# Revit family: РДК-50СВ
name_source: partatom
category: Арматура трубопроводов
units: mm (PartAtom-declared; Revit-internal decimal feet)

## family parameters
Всегда вертикально = Да
На основе рабочей плоскости = Нет
Общий = Нет
При загрузке вырезать с полостями = Нет
Размер круглого соединителя = Использовать диаметр
Тип детали = Клапан - Вставляется

## types (8) — shared parameters
ADSK_Единица измерения = шт.
ADSK_Завод-изготовитель = РУП "БЕЛГАЗТЕХНИКА"
ADSK_Количество = 1
ADSK_Марка = РДК-50СВ
ADSK_Масса_Текст = 24,0 кг
ADSK_Материал наименование = АК-12 ГОСТ 1583-93
ADSK_Тип соединения = фланцевый
zero-valued in all types: Отметка по умолчанию

## per-type parameters (varying)
| type | ADSK_Диапазоны настройки выходного давления, кПа | ADSK_Наименование | направление потока газа Л - влево | направление потока газа П - вправо |
| РДК-50СВ-Л 1,8-10 | 1,8-10 | Регулятор РДК-50СВ-Л-(1,8-10) ТУ BY 100270876.205-2020 | Да | Нет |
| РДК-50СВ-П 1,8-10 | 1,8-10 | Регулятор РДК-50СВ-П-(1,8-10) ТУ BY 100270876.205-2020 | Нет | Да |
| РДК-50СВ-Л 10-50 | 10-50 | Регулятор РДК-50СВ-Л-(10-50) ТУ BY 100270876.205-2020 | Да | Нет |
| РДК-50СВ-П 10-50 | 10-50 | Регулятор РДК-50СВ-П-(10-50) ТУ BY 100270876.205-2020 | Нет | Да |
| РДК-50СВ-Л 50-100 | 50-100 | Регулятор РДК-50СВ-Л-(50-100) ТУ BY 100270876.205-2020 | Да | Нет |
| РДК-50СВ-П 50-100 | 50-100 | Регулятор РДК-50СВ-П-(50-100) ТУ BY 100270876.205-2020 | Нет | Да |
| РДК-50СВ-Л 100-600 | 100-600 | Регулятор РДК-50СВ-Л-(100-600) ТУ BY 100270876.205-2020 | Да | Нет |
| РДК-50СВ-П 100-600 | 100-600 | Регулятор РДК-50СВ-П-(100-600) ТУ BY 100270876.205-2020 | Нет | Да |
